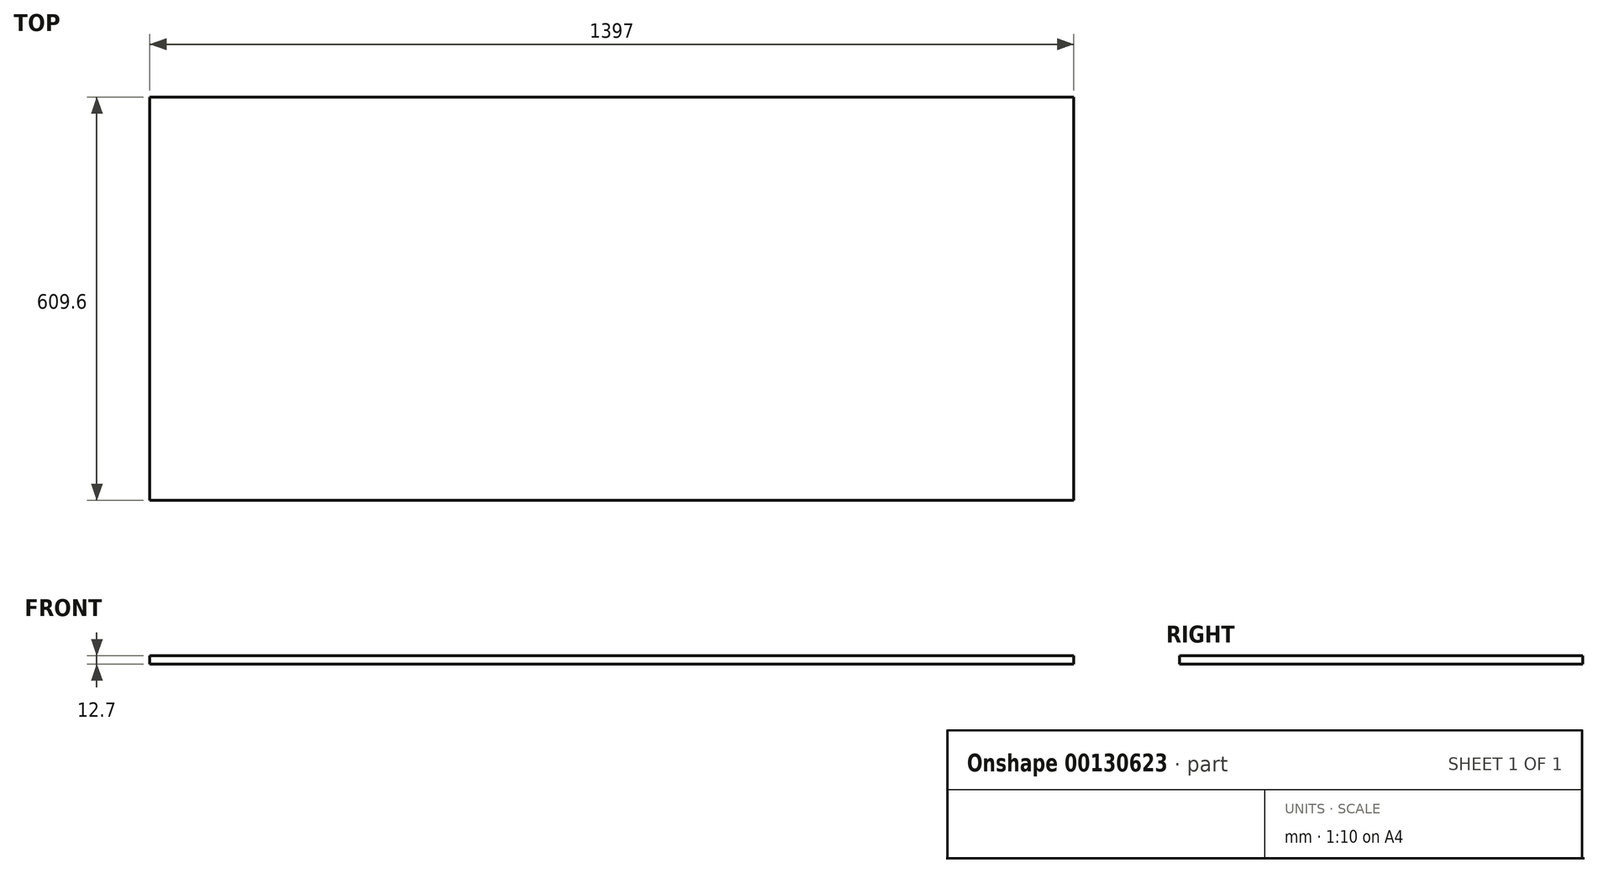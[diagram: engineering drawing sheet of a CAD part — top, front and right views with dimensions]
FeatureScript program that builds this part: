
annotation { "Feature Type Name" : "Feature", "Feature Type Description" : "" }
export const myFeature = defineFeature(function(context is Context, id is Id, definition is map)
    precondition{}
    {
        {
            var Q0;
            Q0=qCreatedBy(makeId("Top.planeOp"),FACE);
            var sketch = newSketch(context, id + "F0", { "sketchPlane" : qUnion([Q0])});
            skLineSegment(sketch, "E0.bottom", {"start": v(0, 0) * mm, "end": v(1397, 0) * mm});
            skLineSegment(sketch, "E0.top", {"start": v(0, 609.6) * mm, "end": v(1397, 609.6) * mm});
            skLineSegment(sketch, "E0.left", {"start": v(0, 0) * mm, "end": v(0, 609.6) * mm});
            skLineSegment(sketch, "E0.right", {"start": v(1397, 0) * mm, "end": v(1397, 609.6) * mm});
            skSolve(sketch);
        }
        {
            var Q0;
            Q0=makeQuery(id+"F0.imprint","IMPRINT",FACE,{"disambiguationData":[TD([[makeQuery(id+"F0.imprint","IMPRINT",EDGE,{"derivedFrom":sQuery(id+"F0.wireOp",EDGE,"E0.bottom")}),1.0]])]});
            extrude(context, id + "F1", {"entities" : qUnion([Q0]), "depth" : 12.7 * mm});
        }
    });
